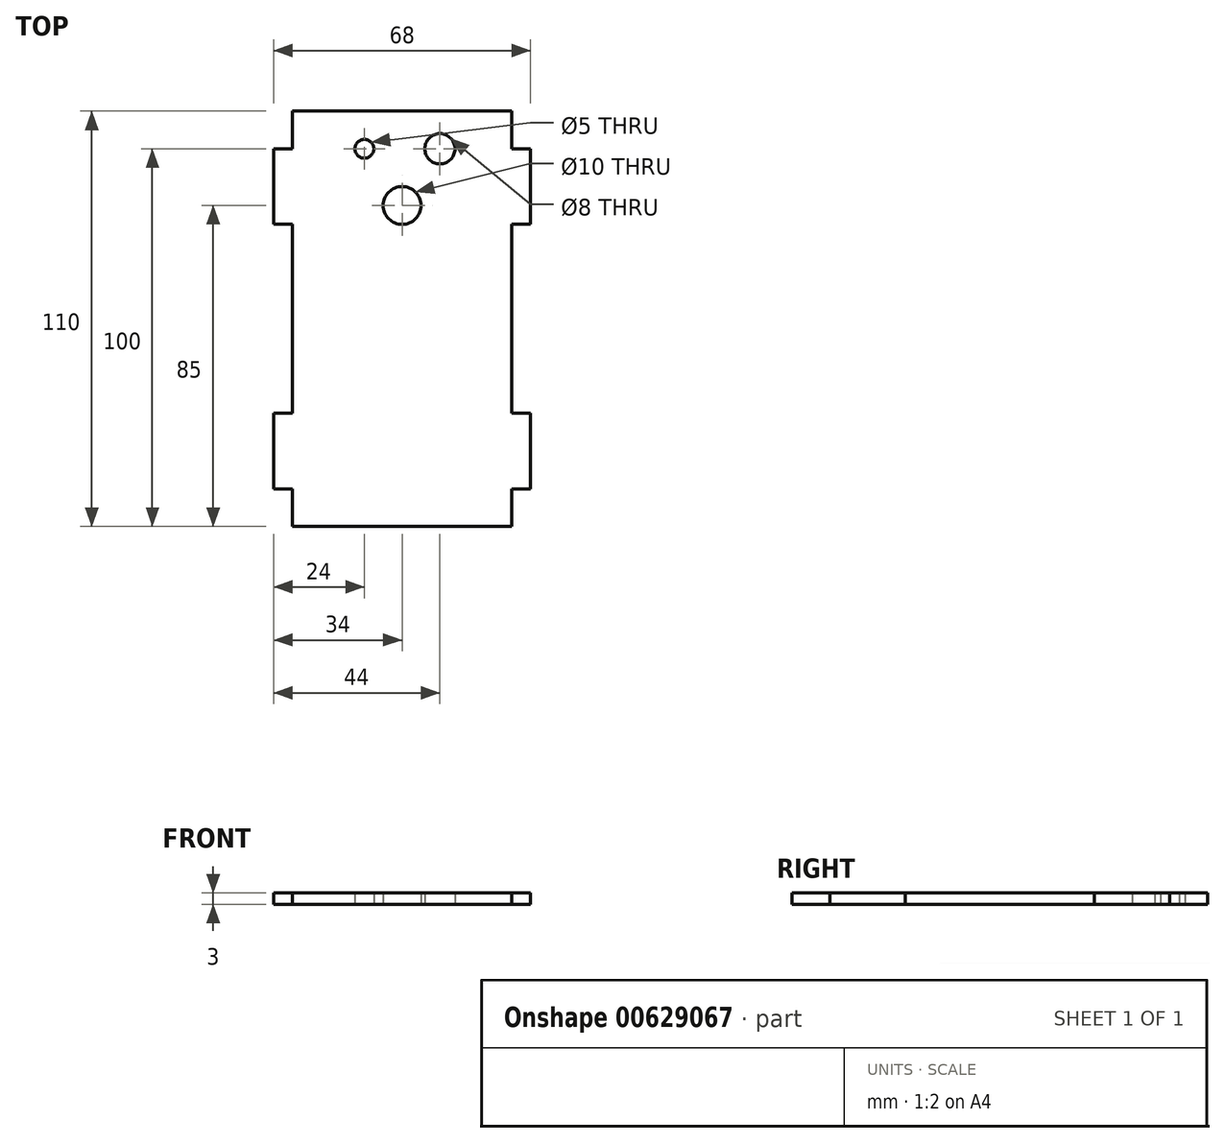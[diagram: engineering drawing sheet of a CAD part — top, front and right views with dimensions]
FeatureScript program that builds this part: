
annotation { "Feature Type Name" : "Feature", "Feature Type Description" : "" }
export const myFeature = defineFeature(function(context is Context, id is Id, definition is map)
    precondition{}
    {
        {
            var Q0;
            Q0=qCreatedBy(makeId("Top.planeOp"),FACE);
            var sketch = newSketch(context, id + "F0", { "sketchPlane" : qUnion([Q0])});
            skLineSegment(sketch, "E0", {"start": v(0, 59.01) * mm, "end": v(0, -67.95) * mm, "construction": true});
            skLineSegment(sketch, "E1", {"start": v(-39.76, 0) * mm, "end": v(41.14, 0) * mm, "construction": true});
            skLineSegment(sketch, "E2.bottom", {"start": v(-29, 55) * mm, "end": v(29, 55) * mm});
            skLineSegment(sketch, "E2.top", {"start": v(-29, -55) * mm, "end": v(29, -55) * mm});
            skLineSegment(sketch, "E2.right", {"start": v(34, 45) * mm, "end": v(34, 25) * mm});
            skLineSegment(sketch, "E3.top", {"start": v(-34, 45) * mm, "end": v(-29, 45) * mm});
            skLineSegment(sketch, "E3.right", {"start": v(-29, 55) * mm, "end": v(-29, 45) * mm});
            skLineSegment(sketch, "E4.bottom", {"start": v(-34, 25) * mm, "end": v(-29, 25) * mm});
            skLineSegment(sketch, "E4.top", {"start": v(-34, -25) * mm, "end": v(-29, -25) * mm});
            skLineSegment(sketch, "E4.right", {"start": v(-29, 25) * mm, "end": v(-29, -25) * mm});
            skLineSegment(sketch, "E5.trimOffspring", {"start": v(-34, 45) * mm, "end": v(-34, 25) * mm});
            skLineSegment(sketch, "E6.trimOffspring", {"start": v(-34, -25) * mm, "end": v(-34, -45) * mm});
            skLineSegment(sketch, "E7.MirrorCS", {"start": v(-29, -55) * mm, "end": v(-29, -45) * mm});
            skLineSegment(sketch, "E8.MirrorCS", {"start": v(-34, -45) * mm, "end": v(-29, -45) * mm});
            skLineSegment(sketch, "E9.MirrorCS", {"start": v(34, -45) * mm, "end": v(29, -45) * mm});
            skLineSegment(sketch, "E10.MirrorCS", {"start": v(34, -25) * mm, "end": v(29, -25) * mm});
            skLineSegment(sketch, "E11.MirrorCS", {"start": v(34, 25) * mm, "end": v(29, 25) * mm});
            skLineSegment(sketch, "E12.MirrorCS", {"start": v(34, 45) * mm, "end": v(29, 45) * mm});
            skLineSegment(sketch, "E13.MirrorCS", {"start": v(29, -55) * mm, "end": v(-29, -55) * mm});
            skLineSegment(sketch, "E14.MirrorCS", {"start": v(29, 55) * mm, "end": v(-29, 55) * mm});
            skLineSegment(sketch, "E15.MirrorCS", {"start": v(39.76, 0) * mm, "end": v(-41.14, 0) * mm, "construction": true});
            skLineSegment(sketch, "E16.MirrorCS", {"start": v(29, -55) * mm, "end": v(29, -45) * mm});
            skLineSegment(sketch, "E17.MirrorCS", {"start": v(34, -25) * mm, "end": v(34, -45) * mm});
            skLineSegment(sketch, "E18.MirrorCS", {"start": v(29, 25) * mm, "end": v(29, -25) * mm});
            skLineSegment(sketch, "E19.MirrorCS", {"start": v(29, 55) * mm, "end": v(29, 45) * mm});
            skLineSegment(sketch, "E20", {"start": v(-20.27, 45) * mm, "end": v(20.66, 45) * mm, "construction": true});
            skCircle(sketch, "E21", {"center": v(0, 30) * mm, "radius": 5 * mm});
            skCircle(sketch, "E22", {"center": v(-10, 45) * mm, "radius": 2.5 * mm});
            skCircle(sketch, "E23", {"center": v(10, 45) * mm, "radius": 4 * mm});
            skSolve(sketch);
        }
        {
            var Q0;
            Q0=qSketchRegion(id+"F0",true);
            extrude(context, id + "F1", {"entities" : qUnion([Q0]), "endBound" : BoundingType.SYMMETRIC, "depth" : 3 * mm, "offsetDistance" : 25 * mm});
        }
    });
